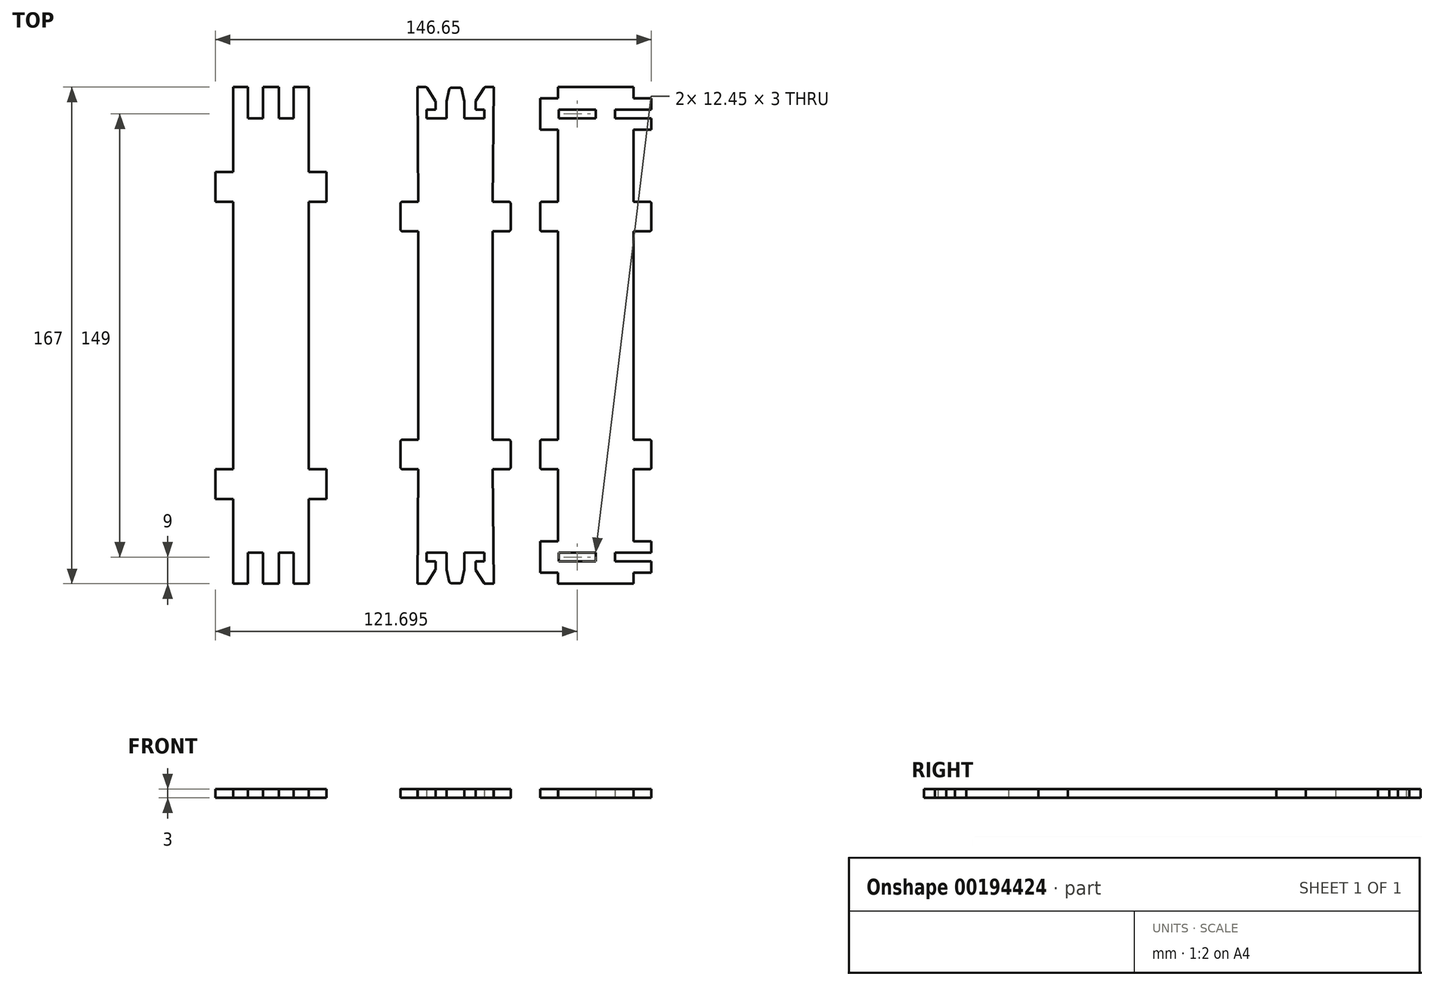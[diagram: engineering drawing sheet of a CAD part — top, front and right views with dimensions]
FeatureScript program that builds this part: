
annotation { "Feature Type Name" : "Feature", "Feature Type Description" : "" }
export const myFeature = defineFeature(function(context is Context, id is Id, definition is map)
    precondition{}
    {
        {
            var Q0;
            Q0=qCreatedBy(makeId("Top.planeOp"),FACE);
            var sketch = newSketch(context, id + "F0", { "sketchPlane" : qUnion([Q0])});
            skLineSegment(sketch, "E0.MirrorCS", {"start": v(-9.7, 76) * mm, "end": v(-6.7, 76) * mm});
            skLineSegment(sketch, "E1.MirrorCS", {"start": v(-6.7, 76) * mm, "end": v(-6.7, 78.56) * mm});
            skLineSegment(sketch, "E2.MirrorCS", {"start": v(-3, 78.75) * mm, "end": v(-3, 73) * mm});
            skLineSegment(sketch, "E3.MirrorCS", {"start": v(-9.7, 76) * mm, "end": v(-9.7, 73) * mm});
            skLineSegment(sketch, "E4.MirrorCS", {"start": v(-9.7, 73) * mm, "end": v(-7.7, 48) * mm});
            skLineSegment(sketch, "E5.MirrorCS", {"start": v(-3, 78.75) * mm, "end": v(-2.1, 82.76) * mm});
            skLineSegment(sketch, "E6.MirrorCS", {"start": v(-3, 73) * mm, "end": v(-9.7, 73) * mm});
            skLineSegment(sketch, "E7", {"start": v(-1.46, 83.28) * mm, "end": v(0, 83.28) * mm});
            skArc(sketch, "E8.filletArc", {"start": v(-1.46, 83.28) * mm, "mid": v(-1.87, 83.14) * mm, "end": v(-2.1, 82.76) * mm});
            skLineSegment(sketch, "E9", {"start": v(-12.78, 83.5) * mm, "end": v(-10.06, 83.5) * mm});
            skLineSegment(sketch, "E10", {"start": v(-9.5, 83.2) * mm, "end": v(-6.8, 78.9) * mm});
            skPoint(sketch, "E11.visualSharp", {"position": v(-9.7, 83.5) * mm});
            skArc(sketch, "E11.filletArc", {"start": v(-9.5, 83.2) * mm, "mid": v(-9.75, 83.42) * mm, "end": v(-10.06, 83.5) * mm});
            skPoint(sketch, "E12.visualSharp", {"position": v(-6.7, 78.75) * mm});
            skArc(sketch, "E12.filletArc", {"start": v(-6.7, 78.56) * mm, "mid": v(-6.73, 78.74) * mm, "end": v(-6.8, 78.9) * mm});
            skLineSegment(sketch, "E13", {"start": v(-12.5, 35) * mm, "end": v(-17.84, 35) * mm});
            skLineSegment(sketch, "E14", {"start": v(-18.5, 35.66) * mm, "end": v(-18.5, 44.34) * mm});
            skLineSegment(sketch, "E15", {"start": v(-17.84, 45) * mm, "end": v(-12.5, 45) * mm});
            skLineSegment(sketch, "E16", {"start": v(-12.5, 35) * mm, "end": v(-12.5, 0) * mm});
            skPoint(sketch, "E17.visualSharp", {"position": v(-18.5, 45) * mm});
            skArc(sketch, "E17.filletArc", {"start": v(-17.84, 45) * mm, "mid": v(-18.3, 44.8) * mm, "end": v(-18.5, 44.34) * mm});
            skPoint(sketch, "E18.visualSharp", {"position": v(-18.5, 35) * mm});
            skArc(sketch, "E18.filletArc", {"start": v(-18.5, 35.66) * mm, "mid": v(-18.3, 35.2) * mm, "end": v(-17.84, 35) * mm});
            skLineSegment(sketch, "E19", {"start": v(-12.78, 83.5) * mm, "end": v(-12.5, 45) * mm});
            skArc(sketch, "E20.MirrorCS", {"start": v(6.7, 78.56) * mm, "mid": v(6.73, 78.74) * mm, "end": v(6.8, 78.9) * mm});
            skArc(sketch, "E21.MirrorCS", {"start": v(18.5, 35.66) * mm, "mid": v(18.3, 35.2) * mm, "end": v(17.84, 35) * mm});
            skLineSegment(sketch, "E22.MirrorCS", {"start": v(1.46, 83.28) * mm, "end": v(0, 83.28) * mm});
            skArc(sketch, "E23.MirrorCS", {"start": v(1.46, 83.28) * mm, "mid": v(1.87, 83.14) * mm, "end": v(2.1, 82.76) * mm});
            skLineSegment(sketch, "E24.MirrorCS", {"start": v(9.5, 83.2) * mm, "end": v(6.8, 78.9) * mm});
            skArc(sketch, "E25.MirrorCS", {"start": v(9.5, 83.2) * mm, "mid": v(9.75, 83.42) * mm, "end": v(10.06, 83.5) * mm});
            skArc(sketch, "E26.MirrorCS", {"start": v(17.84, 45) * mm, "mid": v(18.3, 44.8) * mm, "end": v(18.5, 44.34) * mm});
            skLineSegment(sketch, "E27.MirrorCS", {"start": v(3, 78.75) * mm, "end": v(2.1, 82.76) * mm});
            skLineSegment(sketch, "E28.MirrorCS", {"start": v(12.78, 83.5) * mm, "end": v(10.06, 83.5) * mm});
            skLineSegment(sketch, "E29.MirrorCS", {"start": v(12.5, 35) * mm, "end": v(17.84, 35) * mm});
            skLineSegment(sketch, "E30.MirrorCS", {"start": v(6.7, 76) * mm, "end": v(6.7, 78.56) * mm});
            skLineSegment(sketch, "E31.MirrorCS", {"start": v(9.7, 76) * mm, "end": v(9.7, 73) * mm});
            skLineSegment(sketch, "E32.MirrorCS", {"start": v(9.7, 76) * mm, "end": v(6.7, 76) * mm});
            skLineSegment(sketch, "E33.MirrorCS", {"start": v(17.84, 45) * mm, "end": v(12.5, 45) * mm});
            skLineSegment(sketch, "E34.MirrorCS", {"start": v(9.7, 73) * mm, "end": v(7.7, 48) * mm});
            skPoint(sketch, "E35.MirrorP", {"position": v(18.5, 35) * mm});
            skPoint(sketch, "E36.MirrorP", {"position": v(18.5, 45) * mm});
            skLineSegment(sketch, "E37.MirrorCS", {"start": v(3, 73) * mm, "end": v(9.7, 73) * mm});
            skPoint(sketch, "E38.MirrorP", {"position": v(6.7, 78.75) * mm});
            skLineSegment(sketch, "E39.MirrorCS", {"start": v(3, 78.75) * mm, "end": v(3, 73) * mm});
            skLineSegment(sketch, "E40.MirrorCS", {"start": v(18.5, 35.66) * mm, "end": v(18.5, 44.34) * mm});
            skLineSegment(sketch, "E41.MirrorCS", {"start": v(12.78, 83.5) * mm, "end": v(12.5, 45) * mm});
            skLineSegment(sketch, "E42.MirrorCS", {"start": v(12.5, 35) * mm, "end": v(12.5, 0) * mm});
            skPoint(sketch, "E43.MirrorP", {"position": v(9.7, 83.5) * mm});
            skArc(sketch, "E44.MirrorCS", {"start": v(-6.7, -78.56) * mm, "mid": v(-6.73, -78.74) * mm, "end": v(-6.8, -78.9) * mm});
            skLineSegment(sketch, "E45.MirrorCS", {"start": v(-6.7, -76) * mm, "end": v(-6.7, -78.56) * mm});
            skArc(sketch, "E46.MirrorCS", {"start": v(17.84, -45) * mm, "mid": v(18.3, -44.8) * mm, "end": v(18.5, -44.34) * mm});
            skArc(sketch, "E47.MirrorCS", {"start": v(-17.84, -45) * mm, "mid": v(-18.3, -44.8) * mm, "end": v(-18.5, -44.34) * mm});
            skLineSegment(sketch, "E48.MirrorCS", {"start": v(-9.7, -76) * mm, "end": v(-6.7, -76) * mm});
            skLineSegment(sketch, "E49.MirrorCS", {"start": v(-9.7, -76) * mm, "end": v(-9.7, -73) * mm});
            skArc(sketch, "E50.MirrorCS", {"start": v(6.7, -78.56) * mm, "mid": v(6.73, -78.74) * mm, "end": v(6.8, -78.9) * mm});
            skLineSegment(sketch, "E51.MirrorCS", {"start": v(6.7, -76) * mm, "end": v(6.7, -78.56) * mm});
            skLineSegment(sketch, "E52.MirrorCS", {"start": v(9.7, -76) * mm, "end": v(9.7, -73) * mm});
            skArc(sketch, "E53.MirrorCS", {"start": v(-9.5, -83.2) * mm, "mid": v(-9.75, -83.42) * mm, "end": v(-10.06, -83.5) * mm});
            skArc(sketch, "E54.MirrorCS", {"start": v(-18.5, -35.66) * mm, "mid": v(-18.3, -35.2) * mm, "end": v(-17.84, -35) * mm});
            skArc(sketch, "E55.MirrorCS", {"start": v(18.5, -35.66) * mm, "mid": v(18.3, -35.2) * mm, "end": v(17.84, -35) * mm});
            skLineSegment(sketch, "E56.MirrorCS", {"start": v(12.78, -83.5) * mm, "end": v(10.06, -83.5) * mm});
            skArc(sketch, "E57.MirrorCS", {"start": v(9.5, -83.2) * mm, "mid": v(9.75, -83.42) * mm, "end": v(10.06, -83.5) * mm});
            skArc(sketch, "E58.MirrorCS", {"start": v(-1.46, -83.28) * mm, "mid": v(-1.87, -83.14) * mm, "end": v(-2.1, -82.76) * mm});
            skLineSegment(sketch, "E59.MirrorCS", {"start": v(-1.46, -83.28) * mm, "end": v(0, -83.28) * mm});
            skLineSegment(sketch, "E60.MirrorCS", {"start": v(1.46, -83.28) * mm, "end": v(0, -83.28) * mm});
            skArc(sketch, "E61.MirrorCS", {"start": v(1.46, -83.28) * mm, "mid": v(1.87, -83.14) * mm, "end": v(2.1, -82.76) * mm});
            skLineSegment(sketch, "E62.MirrorCS", {"start": v(-12.78, -83.5) * mm, "end": v(-10.06, -83.5) * mm});
            skLineSegment(sketch, "E63.MirrorCS", {"start": v(-9.5, -83.2) * mm, "end": v(-6.8, -78.9) * mm});
            skLineSegment(sketch, "E64.MirrorCS", {"start": v(9.5, -83.2) * mm, "end": v(6.8, -78.9) * mm});
            skLineSegment(sketch, "E65.MirrorCS", {"start": v(3, -78.75) * mm, "end": v(2.1, -82.76) * mm});
            skLineSegment(sketch, "E66.MirrorCS", {"start": v(-3, -78.75) * mm, "end": v(-2.1, -82.76) * mm});
            skLineSegment(sketch, "E67.MirrorCS", {"start": v(-17.84, -45) * mm, "end": v(-12.5, -45) * mm});
            skLineSegment(sketch, "E68.MirrorCS", {"start": v(12.5, -35) * mm, "end": v(17.84, -35) * mm});
            skLineSegment(sketch, "E69.MirrorCS", {"start": v(-3, -78.75) * mm, "end": v(-3, -73) * mm});
            skLineSegment(sketch, "E70.MirrorCS", {"start": v(-12.5, -35) * mm, "end": v(-17.84, -35) * mm});
            skLineSegment(sketch, "E71.MirrorCS", {"start": v(3, -78.75) * mm, "end": v(3, -73) * mm});
            skLineSegment(sketch, "E72.MirrorCS", {"start": v(17.84, -45) * mm, "end": v(12.5, -45) * mm});
            skLineSegment(sketch, "E73.MirrorCS", {"start": v(9.7, -76) * mm, "end": v(6.7, -76) * mm});
            skLineSegment(sketch, "E74.MirrorCS", {"start": v(-9.7, -73) * mm, "end": v(-7.7, -48) * mm});
            skLineSegment(sketch, "E75.MirrorCS", {"start": v(9.7, -73) * mm, "end": v(7.7, -48) * mm});
            skLineSegment(sketch, "E76.MirrorCS", {"start": v(3, -73) * mm, "end": v(9.7, -73) * mm});
            skPoint(sketch, "E77.MirrorP", {"position": v(18.5, -35) * mm});
            skLineSegment(sketch, "E78.MirrorCS", {"start": v(18.5, -35.66) * mm, "end": v(18.5, -44.34) * mm});
            skLineSegment(sketch, "E79.MirrorCS", {"start": v(12.5, -35) * mm, "end": v(12.5, 0) * mm});
            skPoint(sketch, "E80.MirrorP", {"position": v(-18.5, -35) * mm});
            skPoint(sketch, "E81.MirrorP", {"position": v(-9.7, -83.5) * mm});
            skPoint(sketch, "E82.MirrorP", {"position": v(6.7, -78.75) * mm});
            skPoint(sketch, "E83.MirrorP", {"position": v(-18.5, -45) * mm});
            skLineSegment(sketch, "E84.MirrorCS", {"start": v(-12.78, -83.5) * mm, "end": v(-12.5, -45) * mm});
            skLineSegment(sketch, "E85.MirrorCS", {"start": v(-18.5, -35.66) * mm, "end": v(-18.5, -44.34) * mm});
            skPoint(sketch, "E86.MirrorP", {"position": v(18.5, -45) * mm});
            skPoint(sketch, "E87.MirrorP", {"position": v(-6.7, -78.75) * mm});
            skLineSegment(sketch, "E88.MirrorCS", {"start": v(-12.5, -35) * mm, "end": v(-12.5, 0) * mm});
            skLineSegment(sketch, "E89.MirrorCS", {"start": v(-3, -73) * mm, "end": v(-9.7, -73) * mm});
            skLineSegment(sketch, "E90.MirrorCS", {"start": v(12.78, -83.5) * mm, "end": v(12.5, -45) * mm});
            skPoint(sketch, "E91.MirrorP", {"position": v(9.7, -83.5) * mm});
            skSolve(sketch);
        }
        {
            var Q0;
            Q0=qSketchRegion(id+"F0",true);
            extrude(context, id + "F1", {"entities" : qUnion([Q0]), "depth" : 3 * mm});
        }
        {
            var Q0;
            Q0=qCreatedBy(makeId("Top.planeOp"),FACE);
            var sketch = newSketch(context, id + "F2", { "sketchPlane" : qUnion([Q0])});
            skLineSegment(sketch, "E92.0", {"start": v(29.09, 45) * mm, "end": v(34.43, 45) * mm});
            skLineSegment(sketch, "E93.0", {"start": v(28.43, 35.66) * mm, "end": v(28.43, 44.34) * mm});
            skArc(sketch, "E94.0", {"start": v(29.09, 45) * mm, "mid": v(28.62, 44.8) * mm, "end": v(28.43, 44.34) * mm});
            skArc(sketch, "E95.0", {"start": v(28.43, 35.66) * mm, "mid": v(28.62, 35.2) * mm, "end": v(29.09, 35) * mm});
            skLineSegment(sketch, "E96.0", {"start": v(34.43, 35) * mm, "end": v(29.09, 35) * mm});
            skLineSegment(sketch, "E97", {"start": v(34.43, 45) * mm, "end": v(34.43, 69.25) * mm});
            skLineSegment(sketch, "E98", {"start": v(34.43, 69.25) * mm, "end": v(28.43, 69.25) * mm});
            skLineSegment(sketch, "E99", {"start": v(28.43, 69.25) * mm, "end": v(28.43, 79.75) * mm});
            skLineSegment(sketch, "E100", {"start": v(34.65, 73) * mm, "end": v(47.1, 73) * mm});
            skLineSegment(sketch, "E101", {"start": v(65.83, 73) * mm, "end": v(65.83, 69.25) * mm});
            skArc(sketch, "E102.MirrorCS", {"start": v(65.83, 35.66) * mm, "mid": v(65.63, 35.2) * mm, "end": v(65.16, 35) * mm});
            skArc(sketch, "E103.MirrorCS", {"start": v(65.16, 45) * mm, "mid": v(65.63, 44.8) * mm, "end": v(65.83, 44.34) * mm});
            skLineSegment(sketch, "E104.MirrorCS", {"start": v(59.83, 35) * mm, "end": v(65.16, 35) * mm});
            skLineSegment(sketch, "E105.MirrorCS", {"start": v(65.16, 45) * mm, "end": v(59.83, 45) * mm});
            skLineSegment(sketch, "E106.MirrorCS", {"start": v(65.83, 35.66) * mm, "end": v(65.83, 44.34) * mm});
            skLineSegment(sketch, "E107.MirrorCS", {"start": v(59.83, 45) * mm, "end": v(59.83, 69.25) * mm});
            skLineSegment(sketch, "E108", {"start": v(34.43, 35) * mm, "end": v(34.43, 0) * mm});
            skLineSegment(sketch, "E109", {"start": v(59.83, 35) * mm, "end": v(59.83, 0) * mm});
            skLineSegment(sketch, "E110", {"start": v(47.1, 76) * mm, "end": v(47.1, 73) * mm});
            skLineSegment(sketch, "E111", {"start": v(34.65, 76) * mm, "end": v(34.65, 73) * mm});
            skLineSegment(sketch, "E112", {"start": v(59.83, 69.25) * mm, "end": v(65.83, 69.25) * mm});
            skLineSegment(sketch, "E113", {"start": v(34.65, 76) * mm, "end": v(47.1, 76) * mm});
            skLineSegment(sketch, "E114", {"start": v(28.43, 79.75) * mm, "end": v(34.44, 79.75) * mm});
            skLineSegment(sketch, "E115", {"start": v(34.44, 79.75) * mm, "end": v(34.44, 83.5) * mm});
            skLineSegment(sketch, "E116", {"start": v(34.44, 83.5) * mm, "end": v(59.83, 83.5) * mm});
            skLineSegment(sketch, "E117", {"start": v(59.83, 83.5) * mm, "end": v(59.83, 79.75) * mm});
            skLineSegment(sketch, "E118", {"start": v(59.83, 79.75) * mm, "end": v(65.83, 79.75) * mm});
            skLineSegment(sketch, "E119", {"start": v(65.83, 79.75) * mm, "end": v(65.83, 76) * mm});
            skLineSegment(sketch, "E120", {"start": v(65.83, 76) * mm, "end": v(53.6, 76) * mm});
            skLineSegment(sketch, "E121", {"start": v(53.6, 76) * mm, "end": v(53.6, 73) * mm});
            skLineSegment(sketch, "E122", {"start": v(53.6, 73) * mm, "end": v(65.83, 73) * mm});
            skArc(sketch, "E123.MirrorCS", {"start": v(29.09, -45) * mm, "mid": v(28.62, -44.8) * mm, "end": v(28.43, -44.34) * mm});
            skLineSegment(sketch, "E124.MirrorCS", {"start": v(65.83, -73) * mm, "end": v(65.83, -69.25) * mm});
            skLineSegment(sketch, "E125.MirrorCS", {"start": v(53.6, -76) * mm, "end": v(53.6, -73) * mm});
            skLineSegment(sketch, "E126.MirrorCS", {"start": v(65.83, -79.75) * mm, "end": v(65.83, -76) * mm});
            skLineSegment(sketch, "E127.MirrorCS", {"start": v(28.43, -79.75) * mm, "end": v(34.44, -79.75) * mm});
            skLineSegment(sketch, "E128.MirrorCS", {"start": v(34.44, -79.75) * mm, "end": v(34.44, -83.5) * mm});
            skLineSegment(sketch, "E129.MirrorCS", {"start": v(65.16, -45) * mm, "end": v(59.83, -45) * mm});
            skArc(sketch, "E130.MirrorCS", {"start": v(28.43, -35.66) * mm, "mid": v(28.62, -35.2) * mm, "end": v(29.09, -35) * mm});
            skLineSegment(sketch, "E131.MirrorCS", {"start": v(34.43, -35) * mm, "end": v(29.09, -35) * mm});
            skArc(sketch, "E132.MirrorCS", {"start": v(65.16, -45) * mm, "mid": v(65.63, -44.8) * mm, "end": v(65.83, -44.34) * mm});
            skArc(sketch, "E133.MirrorCS", {"start": v(65.83, -35.66) * mm, "mid": v(65.63, -35.2) * mm, "end": v(65.16, -35) * mm});
            skLineSegment(sketch, "E134.MirrorCS", {"start": v(34.43, -69.25) * mm, "end": v(28.43, -69.25) * mm});
            skLineSegment(sketch, "E135.MirrorCS", {"start": v(34.65, -76) * mm, "end": v(34.65, -73) * mm});
            skLineSegment(sketch, "E136.MirrorCS", {"start": v(59.83, -69.25) * mm, "end": v(65.83, -69.25) * mm});
            skLineSegment(sketch, "E137.MirrorCS", {"start": v(59.83, -83.5) * mm, "end": v(59.83, -79.75) * mm});
            skLineSegment(sketch, "E138.MirrorCS", {"start": v(29.09, -45) * mm, "end": v(34.43, -45) * mm});
            skLineSegment(sketch, "E139.MirrorCS", {"start": v(47.1, -76) * mm, "end": v(47.1, -73) * mm});
            skLineSegment(sketch, "E140.MirrorCS", {"start": v(59.83, -79.75) * mm, "end": v(65.83, -79.75) * mm});
            skLineSegment(sketch, "E141.MirrorCS", {"start": v(59.83, -35) * mm, "end": v(65.16, -35) * mm});
            skLineSegment(sketch, "E142.MirrorCS", {"start": v(65.83, -76) * mm, "end": v(53.6, -76) * mm});
            skLineSegment(sketch, "E143.MirrorCS", {"start": v(53.6, -73) * mm, "end": v(65.83, -73) * mm});
            skLineSegment(sketch, "E144.MirrorCS", {"start": v(59.83, -45) * mm, "end": v(59.83, -69.25) * mm});
            skLineSegment(sketch, "E145.MirrorCS", {"start": v(34.65, -76) * mm, "end": v(47.1, -76) * mm});
            skLineSegment(sketch, "E146.MirrorCS", {"start": v(34.43, -35) * mm, "end": v(34.43, 0) * mm});
            skLineSegment(sketch, "E147.MirrorCS", {"start": v(34.44, -83.5) * mm, "end": v(59.83, -83.5) * mm});
            skLineSegment(sketch, "E148.MirrorCS", {"start": v(65.83, -35.66) * mm, "end": v(65.83, -44.34) * mm});
            skLineSegment(sketch, "E149.MirrorCS", {"start": v(59.83, -35) * mm, "end": v(59.83, 0) * mm});
            skLineSegment(sketch, "E150.MirrorCS", {"start": v(34.43, -45) * mm, "end": v(34.43, -69.25) * mm});
            skLineSegment(sketch, "E151.MirrorCS", {"start": v(28.43, -69.25) * mm, "end": v(28.43, -79.75) * mm});
            skLineSegment(sketch, "E152.MirrorCS", {"start": v(28.43, -35.66) * mm, "end": v(28.43, -44.34) * mm});
            skLineSegment(sketch, "E153.MirrorCS", {"start": v(34.65, -73) * mm, "end": v(47.1, -73) * mm});
            skSolve(sketch);
        }
        {
            var Q0;
            Q0=qSketchRegion(id+"F2",true);
            extrude(context, id + "F3", {"entities" : qUnion([Q0]), "depth" : 3 * mm});
        }
        {
            var Q0;
            Q0=qCreatedBy(makeId("Top.planeOp"),FACE);
            var sketch = newSketch(context, id + "F4", { "sketchPlane" : qUnion([Q0])});
            skLineSegment(sketch, "E154", {"start": v(-74.82, 0) * mm, "end": v(-74.82, 45) * mm});
            skLineSegment(sketch, "E155", {"start": v(-74.82, 45) * mm, "end": v(-80.82, 45) * mm});
            skLineSegment(sketch, "E156", {"start": v(-80.82, 45) * mm, "end": v(-80.82, 55) * mm});
            skLineSegment(sketch, "E157", {"start": v(-80.82, 55) * mm, "end": v(-74.82, 55) * mm});
            skLineSegment(sketch, "E158", {"start": v(-74.82, 55) * mm, "end": v(-74.82, 83.5) * mm});
            skLineSegment(sketch, "E159", {"start": v(-74.82, 83.5) * mm, "end": v(-69.82, 83.5) * mm});
            skLineSegment(sketch, "E160", {"start": v(-69.82, 83.5) * mm, "end": v(-69.82, 73) * mm});
            skLineSegment(sketch, "E161", {"start": v(-69.82, 73) * mm, "end": v(-64.82, 73) * mm});
            skLineSegment(sketch, "E162", {"start": v(-64.82, 73) * mm, "end": v(-64.82, 83.5) * mm});
            skLineSegment(sketch, "E163", {"start": v(-64.82, 83.5) * mm, "end": v(-59.42, 83.5) * mm});
            skLineSegment(sketch, "E164", {"start": v(-59.42, 83.5) * mm, "end": v(-59.42, 73) * mm});
            skLineSegment(sketch, "E165", {"start": v(-59.42, 73) * mm, "end": v(-54.42, 73) * mm});
            skLineSegment(sketch, "E166", {"start": v(-54.42, 73) * mm, "end": v(-54.42, 83.5) * mm});
            skLineSegment(sketch, "E167", {"start": v(-54.42, 83.5) * mm, "end": v(-49.42, 83.5) * mm});
            skLineSegment(sketch, "E168", {"start": v(-49.42, 83.5) * mm, "end": v(-49.42, 55) * mm});
            skLineSegment(sketch, "E169", {"start": v(-49.42, 55) * mm, "end": v(-43.42, 55) * mm});
            skLineSegment(sketch, "E170", {"start": v(-43.42, 55) * mm, "end": v(-43.42, 45) * mm});
            skLineSegment(sketch, "E171", {"start": v(-43.42, 45) * mm, "end": v(-49.42, 45) * mm});
            skLineSegment(sketch, "E172", {"start": v(-49.42, 45) * mm, "end": v(-49.42, 0) * mm});
            skLineSegment(sketch, "E173.MirrorCS", {"start": v(-59.42, -83.5) * mm, "end": v(-59.42, -73) * mm});
            skLineSegment(sketch, "E174.MirrorCS", {"start": v(-59.42, -73) * mm, "end": v(-54.42, -73) * mm});
            skLineSegment(sketch, "E175.MirrorCS", {"start": v(-69.82, -73) * mm, "end": v(-64.82, -73) * mm});
            skLineSegment(sketch, "E176.MirrorCS", {"start": v(-80.82, -55) * mm, "end": v(-74.82, -55) * mm});
            skLineSegment(sketch, "E177.MirrorCS", {"start": v(-43.42, -45) * mm, "end": v(-49.42, -45) * mm});
            skLineSegment(sketch, "E178.MirrorCS", {"start": v(-54.42, -83.5) * mm, "end": v(-49.42, -83.5) * mm});
            skLineSegment(sketch, "E179.MirrorCS", {"start": v(-74.82, -45) * mm, "end": v(-80.82, -45) * mm});
            skLineSegment(sketch, "E180.MirrorCS", {"start": v(-74.82, -83.5) * mm, "end": v(-69.82, -83.5) * mm});
            skLineSegment(sketch, "E181.MirrorCS", {"start": v(-54.42, -73) * mm, "end": v(-54.42, -83.5) * mm});
            skLineSegment(sketch, "E182.MirrorCS", {"start": v(-49.42, -55) * mm, "end": v(-43.42, -55) * mm});
            skLineSegment(sketch, "E183.MirrorCS", {"start": v(-64.82, -73) * mm, "end": v(-64.82, -83.5) * mm});
            skLineSegment(sketch, "E184.MirrorCS", {"start": v(-69.82, -83.5) * mm, "end": v(-69.82, -73) * mm});
            skLineSegment(sketch, "E185.MirrorCS", {"start": v(-64.82, -83.5) * mm, "end": v(-59.42, -83.5) * mm});
            skLineSegment(sketch, "E186.MirrorCS", {"start": v(-49.42, -83.5) * mm, "end": v(-49.42, -55) * mm});
            skLineSegment(sketch, "E187.MirrorCS", {"start": v(-80.82, -45) * mm, "end": v(-80.82, -55) * mm});
            skLineSegment(sketch, "E188.MirrorCS", {"start": v(-49.42, -45) * mm, "end": v(-49.42, 0) * mm});
            skLineSegment(sketch, "E189.MirrorCS", {"start": v(-74.82, -55) * mm, "end": v(-74.82, -83.5) * mm});
            skLineSegment(sketch, "E190.MirrorCS", {"start": v(-74.82, 0) * mm, "end": v(-74.82, -45) * mm});
            skLineSegment(sketch, "E191.MirrorCS", {"start": v(-43.42, -55) * mm, "end": v(-43.42, -45) * mm});
            skSolve(sketch);
        }
        {
            var Q0;
            Q0=makeQuery(id+"F4.imprint","IMPRINT",FACE,{"disambiguationData":[TD([[makeQuery(id+"F4.imprint","IMPRINT",EDGE,{"derivedFrom":sQuery(id+"F4.wireOp",EDGE,"E154")}),-1.0]])]});
            extrude(context, id + "F5", {"entities" : qUnion([Q0]), "depth" : 3 * mm});
        }
    });
